# Revit family: NLRS_63_LF_UN_noodverlichting multled Stelar inbouw_hertek
name_source: partatom
category: Lighting Fixtures
units: mm (PartAtom-declared; Revit-internal decimal feet)

## family parameters
Always vertical = No
Cut with Voids When Loaded = No
Light Source = No
OmniClass Number = 23.85.30.21
OmniClass Title = Environmental Detection/Registration
Part Type = Normal
Room Calculation Point = Yes
Round Connector Dimension = Use Diameter
Shared = Yes
Work Plane-Based = No

## types (1)
- Multiled Stelar Series 3 dec AT inbouw wit_decentraal _hertek_NJD418-4
    Default Elevation = 0 mm  [stored 0 ft]
    Lamp = LED
    Manufacturer = Hertek
    NLRS_C_breedte = 92 mm  [stored 0.301837 ft]
    NLRS_C_code_ETIM = EC001957
    NLRS_C_code_ETIM_url = http://prod.etim-international.com
    NLRS_C_code_artikel = NJD418-4
    NLRS_C_code_fabrikant_gln = 8714253082646
    NLRS_C_hoogte = 97 mm  [stored 0.318241 ft]
    NLRS_C_lengte = 92 mm  [stored 0.301837 ft]
    NLRS_C_materiaal = Staal-wit (RAL9003)
    NLRS_C_materiaal_kleur = RAL9003
    NLRS_C_model = Multiled Stelar Series 3
    NLRS_C_omschrijving = Multiled Stelar Series 3 dec AT inbouw wit LiFePo4 10/8YW
    NLRS_C_revit_versie = 2020
    NLRS_E_IPwaarde = 20
    NLRS_E_c01_schijnbaar_vermogen = 5 VA
    NLRS_E_c01_schijnbaar_vermogen_fase_1 = 0 VA
    NLRS_E_c01_schijnbaar_vermogen_fase_2 = 0 VA
    NLRS_E_c01_schijnbaar_vermogen_fase_3 = 0 VA
    NLRS_E_spanning = 230 V
    NLRS_E_stroom = 0.0 A
    NLRS_S_gewicht_netto = 1.40 kg
    Type Comments = Decentraal noodverlichtingarmatuur met volgende specificaties:

Type armatuur		: Multiled Stelar Series-3
Producent/leverancier	: Hertek 
Functie			: Vluchtrouteaanduiding
Materiaal behuizing	                : Gecoat staal 
Uitvoering voor		: Perspex pictogramplaten
Montagewijze		: Inbouw  
Kleur			: RAL 9003 Wit
Voorzien van		: Volautomatische zelftest Voedingsspanning	                : 230VAC  
Functie			: Continue 
Opgenomen vermogen	: 3,5 Watt 
Type lichtbron		: 20 stuks laag vermogen LED’s 
Lichtstroom nominaal	: 150 lumen 
Lichtstroom in nood	                : 150 lumen 
Autonomietijd		: 1 uur 
Batterij			: LiFePO4
Afmetingen		: 300x170x92 mm (bxhxd)
Gewicht		                :  
Water- & stofdichtheid	: IP 20  
Garantie: 10 jaar op het armatuur en 8 jaar op de batterij

LET OP: Armatuur wordt geleverd exclusief pictogramplaat.  Deze dient los besteld te worden!
    Wattage Comments = 5W
    centraal = No
    decentraal = Yes
    vermogensclassificatie = NV
    voorschakelapparaat = NLRS_63_LF_UN_voorschakelapparaat_hertek : spotlux 230v decentraal _hertek

note: [stored X ft] marks values corroborated as IEEE doubles in the binary element streams (Revit-internal decimal feet)

## geometry (parser evidence)
native form markers: Blend x30, Sweep x25
no freeform markers — native parametric forms only
